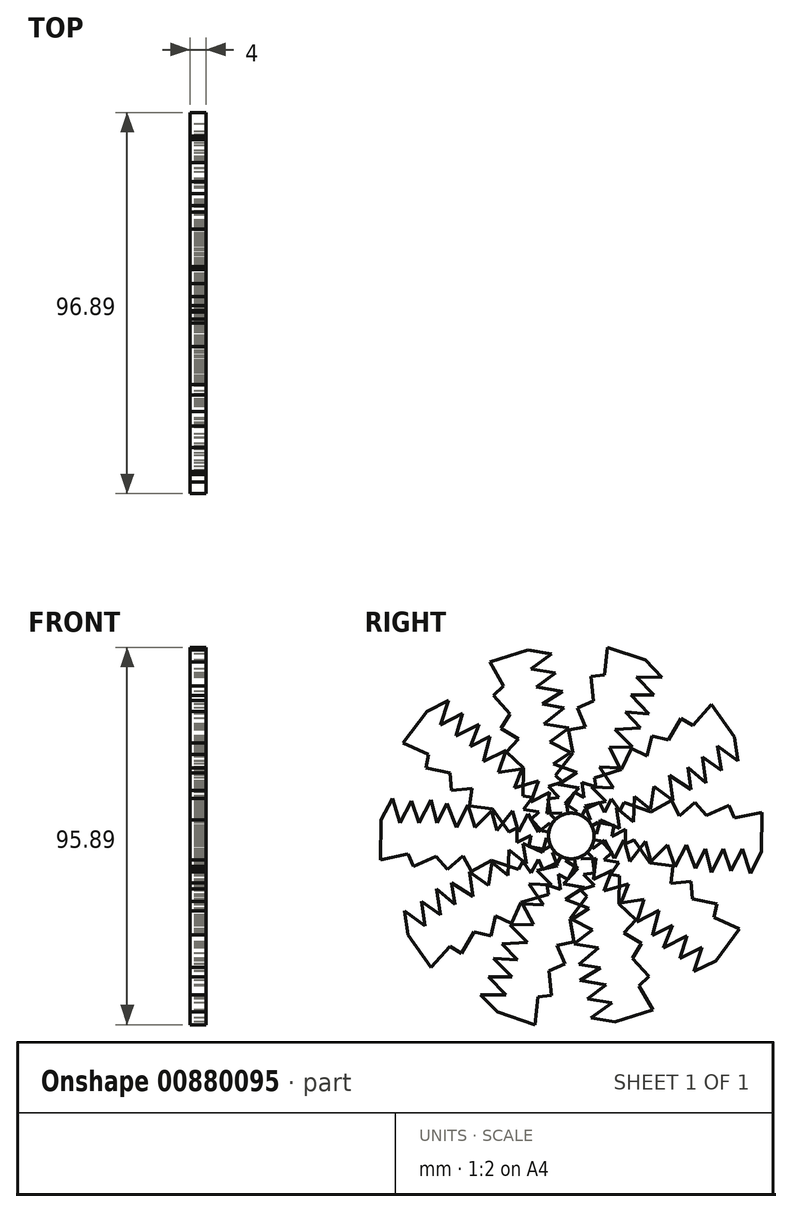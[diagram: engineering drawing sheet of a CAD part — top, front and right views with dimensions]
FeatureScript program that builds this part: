
annotation { "Feature Type Name" : "Feature", "Feature Type Description" : "" }
export const myFeature = defineFeature(function(context is Context, id is Id, definition is map)
    precondition{}
    {
        {
            var Q0;
            Q0=qCreatedBy(makeId("Right.planeOp"),FACE);
            var sketch = newSketch(context, id + "F0", { "sketchPlane" : qUnion([Q0])});
            skLineSegment(sketch, "E0", {"start": v(64.04, -37.62) * mm, "end": v(61.2, -43.05) * mm});
            skLineSegment(sketch, "E1", {"start": v(61.2, -43.05) * mm, "end": v(59.23, -36.88) * mm});
            skLineSegment(sketch, "E2", {"start": v(59.23, -36.88) * mm, "end": v(56.32, -42.46) * mm});
            skLineSegment(sketch, "E3", {"start": v(56.32, -42.46) * mm, "end": v(54.42, -36.88) * mm});
            skLineSegment(sketch, "E4", {"start": v(54.42, -36.88) * mm, "end": v(51.35, -42.76) * mm});
            skLineSegment(sketch, "E5", {"start": v(51.35, -42.76) * mm, "end": v(49.86, -36.88) * mm});
            skLineSegment(sketch, "E6", {"start": v(49.86, -36.88) * mm, "end": v(47.28, -41.82) * mm});
            skLineSegment(sketch, "E7", {"start": v(47.28, -41.82) * mm, "end": v(44.93, -35.77) * mm});
            skLineSegment(sketch, "E8", {"start": v(44.93, -35.77) * mm, "end": v(41.99, -41.4) * mm});
            skLineSegment(sketch, "E9", {"start": v(41.99, -41.4) * mm, "end": v(40.13, -35.77) * mm});
            skLineSegment(sketch, "E10", {"start": v(40.13, -35.77) * mm, "end": v(35.93, -39.97) * mm});
            skLineSegment(sketch, "E11", {"start": v(35.93, -39.97) * mm, "end": v(34.58, -34.91) * mm});
            skLineSegment(sketch, "E12", {"start": v(34.58, -34.91) * mm, "end": v(30.63, -39.97) * mm});
            skLineSegment(sketch, "E13", {"start": v(30.63, -39.97) * mm, "end": v(29.15, -34.54) * mm});
            skLineSegment(sketch, "E14", {"start": v(29.15, -34.54) * mm, "end": v(26.72, -39.2) * mm});
            skLineSegment(sketch, "E15", {"start": v(26.72, -39.2) * mm, "end": v(24.1, -34.54) * mm});
            skLineSegment(sketch, "E16", {"start": v(24.1, -34.54) * mm, "end": v(21.14, -36.88) * mm});
            skLineSegment(sketch, "E17", {"start": v(21.14, -36.88) * mm, "end": v(20.03, -33.06) * mm});
            skLineSegment(sketch, "E18", {"start": v(20.03, -33.06) * mm, "end": v(15.72, -36.88) * mm});
            skLineSegment(sketch, "E19", {"start": v(15.72, -36.88) * mm, "end": v(15.72, -33.56) * mm});
            skLineSegment(sketch, "E20", {"start": v(19.24, -26.81) * mm, "end": v(22.87, -25.05) * mm});
            skLineSegment(sketch, "E21", {"start": v(22.87, -25.05) * mm, "end": v(24.1, -27.58) * mm});
            skLineSegment(sketch, "E22", {"start": v(24.1, -27.58) * mm, "end": v(25.91, -24.12) * mm});
            skLineSegment(sketch, "E23", {"start": v(25.91, -24.12) * mm, "end": v(28.04, -27.15) * mm});
            skLineSegment(sketch, "E24", {"start": v(28.04, -27.15) * mm, "end": v(29.15, -25.02) * mm});
            skLineSegment(sketch, "E25", {"start": v(29.15, -25.02) * mm, "end": v(35.93, -27.4) * mm});
            skLineSegment(sketch, "E26", {"start": v(35.93, -27.4) * mm, "end": v(41.11, -24.56) * mm});
            skLineSegment(sketch, "E27", {"start": v(41.11, -24.56) * mm, "end": v(43.24, -28.44) * mm});
            skLineSegment(sketch, "E28", {"start": v(43.24, -28.44) * mm, "end": v(47.15, -25.05) * mm});
            skLineSegment(sketch, "E29", {"start": v(47.15, -25.05) * mm, "end": v(50.04, -28.38) * mm});
            skLineSegment(sketch, "E30", {"start": v(50.04, -28.38) * mm, "end": v(55.78, -25.79) * mm});
            skLineSegment(sketch, "E31", {"start": v(55.78, -25.79) * mm, "end": v(57.22, -28.97) * mm});
            skLineSegment(sketch, "E32", {"start": v(57.22, -28.97) * mm, "end": v(64.16, -27.52) * mm});
            skLineSegment(sketch, "E33", {"start": v(64.16, -27.52) * mm, "end": v(64.04, -37.62) * mm});
            skLineSegment(sketch, "E34", {"start": v(15.72, -33.56) * mm, "end": v(19.24, -26.81) * mm});
            skSolve(sketch);
        }
        {
            var Q0;
            Q0=makeQuery(id+"F0.imprint","IMPRINT",FACE,{"disambiguationData":[TD([[makeQuery(id+"F0.imprint","IMPRINT",EDGE,{"derivedFrom":sQuery(id+"F0.wireOp",EDGE,"E0")}),-1.0]])]});
            extrude(context, id + "F1", {"entities" : qUnion([Q0]), "depth" : 4 * mm, "offsetDistance" : 25 * mm});
        }
        {
            var Q0;
            Q0=makeQuery(id+"F1.opExtrude","SWEPT_BODY",BODY,{"disambiguationData":[OSD([sQuery(id+"F0.wireOp",EDGE,"E0"),sQuery(id+"F0.wireOp",EDGE,"E1"),sQuery(id+"F0.wireOp",EDGE,"E2"),sQuery(id+"F0.wireOp",EDGE,"E3"),sQuery(id+"F0.wireOp",EDGE,"E4"),sQuery(id+"F0.wireOp",EDGE,"E5"),sQuery(id+"F0.wireOp",EDGE,"E6"),sQuery(id+"F0.wireOp",EDGE,"E7"),sQuery(id+"F0.wireOp",EDGE,"E8"),sQuery(id+"F0.wireOp",EDGE,"E9"),sQuery(id+"F0.wireOp",EDGE,"E10"),sQuery(id+"F0.wireOp",EDGE,"E11"),sQuery(id+"F0.wireOp",EDGE,"E12"),sQuery(id+"F0.wireOp",EDGE,"E13"),sQuery(id+"F0.wireOp",EDGE,"E14"),sQuery(id+"F0.wireOp",EDGE,"E15"),sQuery(id+"F0.wireOp",EDGE,"E16"),sQuery(id+"F0.wireOp",EDGE,"E17"),sQuery(id+"F0.wireOp",EDGE,"E18"),sQuery(id+"F0.wireOp",EDGE,"E19"),sQuery(id+"F0.wireOp",EDGE,"E20"),sQuery(id+"F0.wireOp",EDGE,"E21"),sQuery(id+"F0.wireOp",EDGE,"E22"),sQuery(id+"F0.wireOp",EDGE,"E23"),sQuery(id+"F0.wireOp",EDGE,"E24"),sQuery(id+"F0.wireOp",EDGE,"E25"),sQuery(id+"F0.wireOp",EDGE,"E26"),sQuery(id+"F0.wireOp",EDGE,"E27"),sQuery(id+"F0.wireOp",EDGE,"E28"),sQuery(id+"F0.wireOp",EDGE,"E29"),sQuery(id+"F0.wireOp",EDGE,"E30"),sQuery(id+"F0.wireOp",EDGE,"E31"),sQuery(id+"F0.wireOp",EDGE,"E32"),sQuery(id+"F0.wireOp",EDGE,"E33"),sQuery(id+"F0.wireOp",EDGE,"E34")])]});
            var Q1;
            Q1=makeQuery(id+"F1.opExtrude","SWEPT_EDGE",EDGE,{"disambiguationData":[OSD([sQuery(id+"F0.wireOp",EDGE,"E19"),sQuery(id+"F0.wireOp",EDGE,"E34")])]});
            circularPattern(context, id + "F2", {"entities" : qUnion([Q0]), "axis" : qUnion([Q1]), "angle" : 360 * degree, "instanceCount" : 10, "equalSpace" : true});
        }
        {
            var Q0;
            Q0=makeQuery(id+"F2.opPattern","COPY",FACE,{"derivedFrom":makeQuery(id+"F1.opExtrude","CAP_FACE",FACE,{"disambiguationData":[OSD([sQuery(id+"F0.wireOp",EDGE,"E0"),sQuery(id+"F0.wireOp",EDGE,"E1"),sQuery(id+"F0.wireOp",EDGE,"E2"),sQuery(id+"F0.wireOp",EDGE,"E3"),sQuery(id+"F0.wireOp",EDGE,"E4"),sQuery(id+"F0.wireOp",EDGE,"E5"),sQuery(id+"F0.wireOp",EDGE,"E6"),sQuery(id+"F0.wireOp",EDGE,"E7"),sQuery(id+"F0.wireOp",EDGE,"E8"),sQuery(id+"F0.wireOp",EDGE,"E9"),sQuery(id+"F0.wireOp",EDGE,"E10"),sQuery(id+"F0.wireOp",EDGE,"E11"),sQuery(id+"F0.wireOp",EDGE,"E12"),sQuery(id+"F0.wireOp",EDGE,"E13"),sQuery(id+"F0.wireOp",EDGE,"E14"),sQuery(id+"F0.wireOp",EDGE,"E15"),sQuery(id+"F0.wireOp",EDGE,"E16"),sQuery(id+"F0.wireOp",EDGE,"E17"),sQuery(id+"F0.wireOp",EDGE,"E18"),sQuery(id+"F0.wireOp",EDGE,"E19"),sQuery(id+"F0.wireOp",EDGE,"E20"),sQuery(id+"F0.wireOp",EDGE,"E21"),sQuery(id+"F0.wireOp",EDGE,"E22"),sQuery(id+"F0.wireOp",EDGE,"E23"),sQuery(id+"F0.wireOp",EDGE,"E24"),sQuery(id+"F0.wireOp",EDGE,"E25"),sQuery(id+"F0.wireOp",EDGE,"E26"),sQuery(id+"F0.wireOp",EDGE,"E27"),sQuery(id+"F0.wireOp",EDGE,"E28"),sQuery(id+"F0.wireOp",EDGE,"E29"),sQuery(id+"F0.wireOp",EDGE,"E30"),sQuery(id+"F0.wireOp",EDGE,"E31"),sQuery(id+"F0.wireOp",EDGE,"E32"),sQuery(id+"F0.wireOp",EDGE,"E33"),sQuery(id+"F0.wireOp",EDGE,"E34")])],"isStart":true}),"instanceName":"1"});
            var sketch = newSketch(context, id + "F3", { "sketchPlane" : qUnion([Q0])});
            skCircle(sketch, "E35", {"center": v(-15.72, -33.56) * mm, "radius": 5.8 * mm});
            skSolve(sketch);
        }
        {
            var Q0;
            Q0 = qSketchRegion(id + "F3", true);
            extrude(context, id + "F4", {"entities" : qUnion([Q0]), "operationType" : NewBodyOperationType.REMOVE, "oppositeDirection" : true, "depth" : 25 * mm, "offsetDistance" : 25 * mm});
        }
    });
